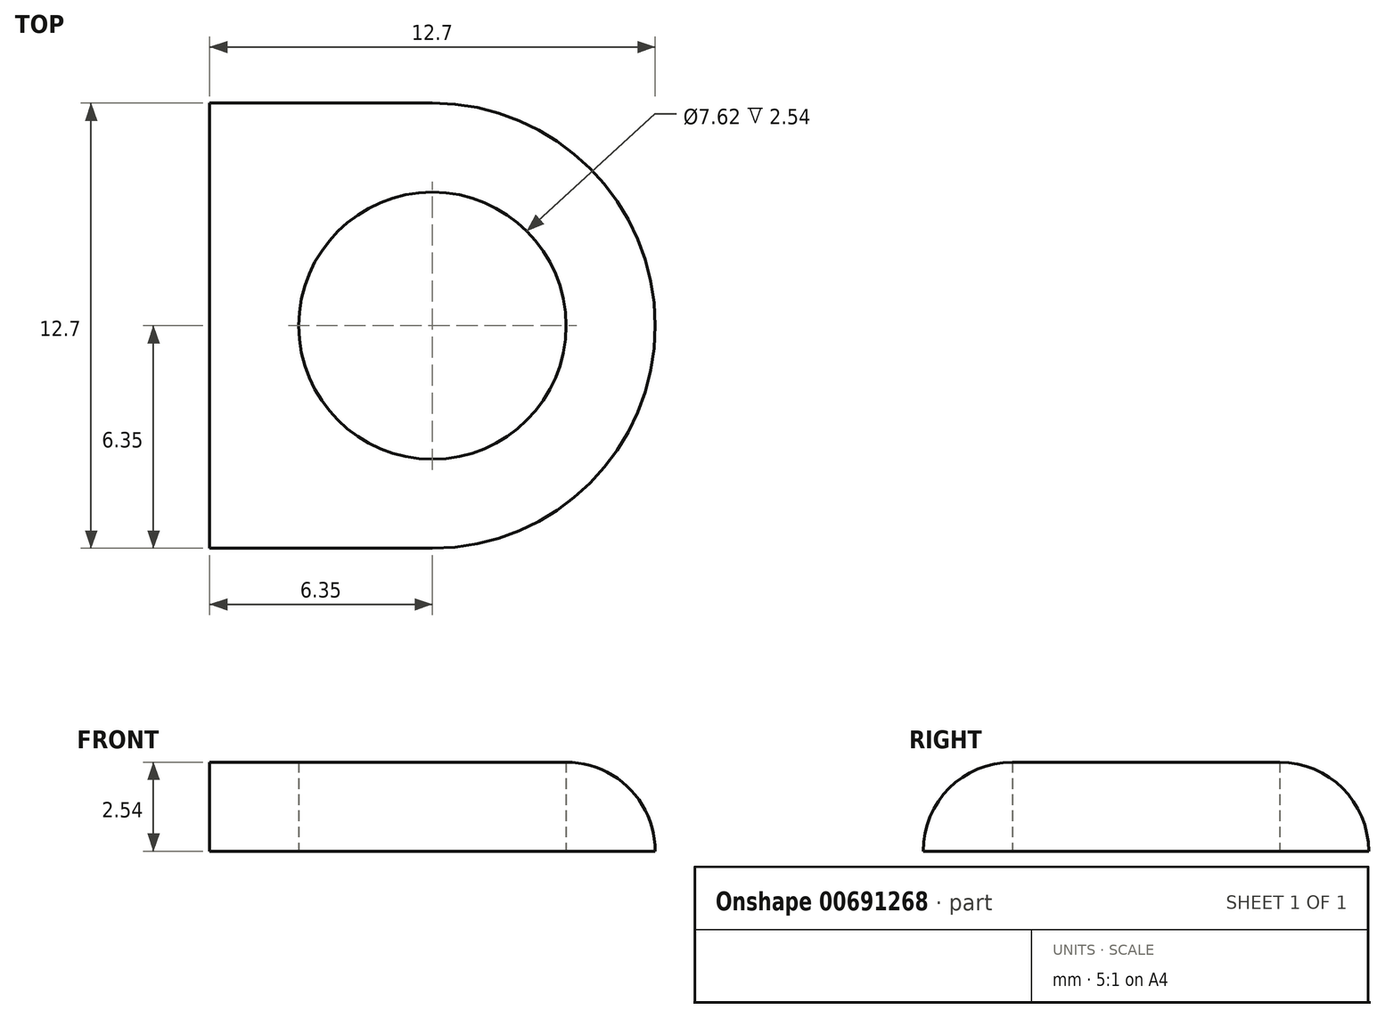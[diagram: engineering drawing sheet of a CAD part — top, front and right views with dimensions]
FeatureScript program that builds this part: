
annotation { "Feature Type Name" : "Feature", "Feature Type Description" : "" }
export const myFeature = defineFeature(function(context is Context, id is Id, definition is map)
    precondition{}
    {
        {
            var Q0;
            Q0=qCreatedBy(makeId("Top.planeOp"),FACE);
            var sketch = newSketch(context, id + "F0", { "sketchPlane" : qUnion([Q0])});
            skCircle(sketch, "E0", {"center": v(0, 0) * mm, "radius": 6.35 * mm});
            skLineSegment(sketch, "E1", {"start": v(0, 0) * mm, "end": v(-6.35, 0) * mm});
            skLineSegment(sketch, "E2", {"start": v(-6.35, 0) * mm, "end": v(-6.35, 6.35) * mm});
            skLineSegment(sketch, "E3", {"start": v(-6.35, 6.35) * mm, "end": v(0, 6.35) * mm});
            skLineSegment(sketch, "E4", {"start": v(-6.35, 0) * mm, "end": v(-6.35, -6.35) * mm});
            skLineSegment(sketch, "E5", {"start": v(-6.35, -6.35) * mm, "end": v(0, -6.35) * mm});
            skCircle(sketch, "E6", {"center": v(0, 0) * mm, "radius": 3.81 * mm});
            skSolve(sketch);
        }
        {
            var Q0;
            Q0 = qSketchRegion(id + "F0", true);
            extrude(context, id + "F1", {"entities" : qUnion([Q0]), "depth" : 2.54 * mm, "offsetDistance" : 25.4 * mm});
        }
        {
            var Q0;
            Q0=makeQuery(id+"F1.opExtrude","CAP_EDGE",EDGE,{"disambiguationData":[OSD([sQuery(id+"F0.wireOp",EDGE,"E3")])],"isStart":false});
            fillet(context, id + "F2", {"entities" : qUnion([Q0]), "radius" : 2.54 * mm, "tangentPropagation" : true, "allowEdgeOverflow" : false});
        }
    });
